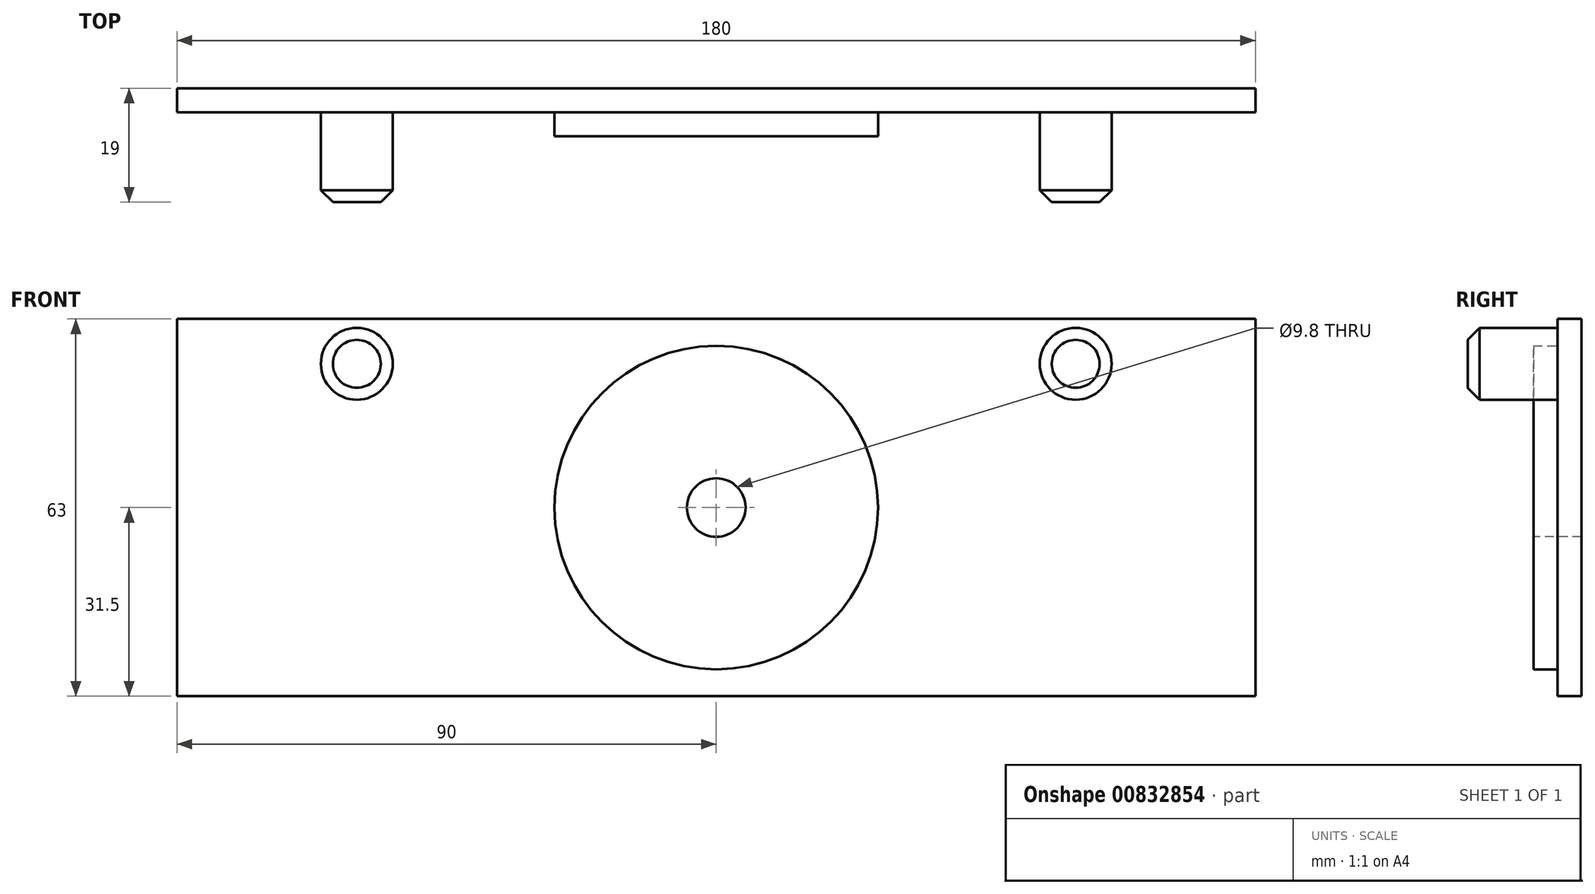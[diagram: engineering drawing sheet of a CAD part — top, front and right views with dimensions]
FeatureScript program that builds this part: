
annotation { "Feature Type Name" : "Feature", "Feature Type Description" : "" }
export const myFeature = defineFeature(function(context is Context, id is Id, definition is map)
    precondition{}
    {
        {
            var Q0;
            Q0=qCreatedBy(makeId("Front.planeOp"),FACE);
            var sketch = newSketch(context, id + "F0", { "sketchPlane" : qUnion([Q0])});
            skLineSegment(sketch, "E0.bottom", {"start": v(0, 0) * mm, "end": v(180, 0) * mm});
            skLineSegment(sketch, "E0.top", {"start": v(0, -63) * mm, "end": v(180, -63) * mm});
            skLineSegment(sketch, "E0.left", {"start": v(0, 0) * mm, "end": v(0, -63) * mm});
            skLineSegment(sketch, "E0.right", {"start": v(180, 0) * mm, "end": v(180, -63) * mm});
            skSolve(sketch);
        }
        {
            var Q0;
            Q0 = qSketchRegion(id + "F0", true);
            extrude(context, id + "F1", {"entities" : qUnion([Q0]), "depth" : 4 * mm, "offsetDistance" : 25 * mm});
        }
        {
            var Q0;
            Q0=makeQuery(id+"F1.opExtrude","CAP_FACE",FACE,{"disambiguationData":[OSD([sQuery(id+"F0.wireOp",EDGE,"E0.bottom"),sQuery(id+"F0.wireOp",EDGE,"E0.top"),sQuery(id+"F0.wireOp",EDGE,"E0.left"),sQuery(id+"F0.wireOp",EDGE,"E0.right")])],"isStart":false});
            var sketch = newSketch(context, id + "F2", { "sketchPlane" : qUnion([Q0])});
            skCircle(sketch, "E1", {"center": v(90, -31.5) * mm, "radius": 27 * mm});
            skCircle(sketch, "E2", {"center": v(30, -7.5) * mm, "radius": 6 * mm});
            skCircle(sketch, "E3", {"center": v(150, -7.5) * mm, "radius": 6 * mm});
            skLineSegment(sketch, "E4", {"start": v(30, -7.5) * mm, "end": v(0, -7.5) * mm, "construction": true});
            skLineSegment(sketch, "E5", {"start": v(150, -7.5) * mm, "end": v(180, -7.5) * mm, "construction": true});
            skSolve(sketch);
        }
        {
            var Q0;
            Q0=makeQuery(id+"F2.imprint","IMPRINT",FACE,{"disambiguationData":[TD([[makeQuery(id+"F2.imprint","IMPRINT",EDGE,{"derivedFrom":sQuery(id+"F2.wireOp",EDGE,"E1")}),1.0]])]});
            extrude(context, id + "F3", {"entities" : qUnion([Q0]), "operationType" : NewBodyOperationType.ADD, "depth" : 4 * mm, "offsetDistance" : 25 * mm});
        }
        {
            var Q0;
            Q0=makeQuery(id+"F2.imprint","IMPRINT",FACE,{"disambiguationData":[TD([[makeQuery(id+"F2.imprint","IMPRINT",EDGE,{"derivedFrom":sQuery(id+"F2.wireOp",EDGE,"E2")}),1.0]])]});
            var Q1;
            Q1=makeQuery(id+"F2.imprint","IMPRINT",FACE,{"disambiguationData":[TD([[makeQuery(id+"F2.imprint","IMPRINT",EDGE,{"derivedFrom":sQuery(id+"F2.wireOp",EDGE,"E3")}),1.0]])]});
            extrude(context, id + "F4", {"entities" : qUnion([Q0, Q1]), "operationType" : NewBodyOperationType.ADD, "depth" : 15 * mm, "offsetDistance" : 25 * mm});
        }
        {
            var Q0;
            Q0=makeQuery(id+"F4.opExtrude","CAP_EDGE",EDGE,{"disambiguationData":[OSD([sQuery(id+"F2.wireOp",EDGE,"E2")])],"isStart":false});
            var Q1;
            Q1=makeQuery(id+"F4.opExtrude","CAP_EDGE",EDGE,{"disambiguationData":[OSD([sQuery(id+"F2.wireOp",EDGE,"E3")])],"isStart":false});
            chamfer(context, id + "F5", {"entities" : qUnion([Q0, Q1]), "width" : 2 * mm, "tangentPropagation" : true});
        }
        {
            var Q0;
            Q0=makeQuery(id+"F3.opExtrude","CAP_FACE",FACE,{"disambiguationData":[OSD([sQuery(id+"F2.wireOp",EDGE,"E1")])],"isStart":false});
            var sketch = newSketch(context, id + "F6", { "sketchPlane" : qUnion([Q0])});
            skCircle(sketch, "E6", {"center": v(90, -31.5) * mm, "radius": 4.9 * mm});
            skSolve(sketch);
        }
        {
            var Q0;
            Q0 = qSketchRegion(id + "F6", true);
            extrude(context, id + "F7", {"entities" : qUnion([Q0]), "operationType" : NewBodyOperationType.REMOVE, "oppositeDirection" : true, "depth" : 25 * mm, "offsetDistance" : 25 * mm});
        }
    });
